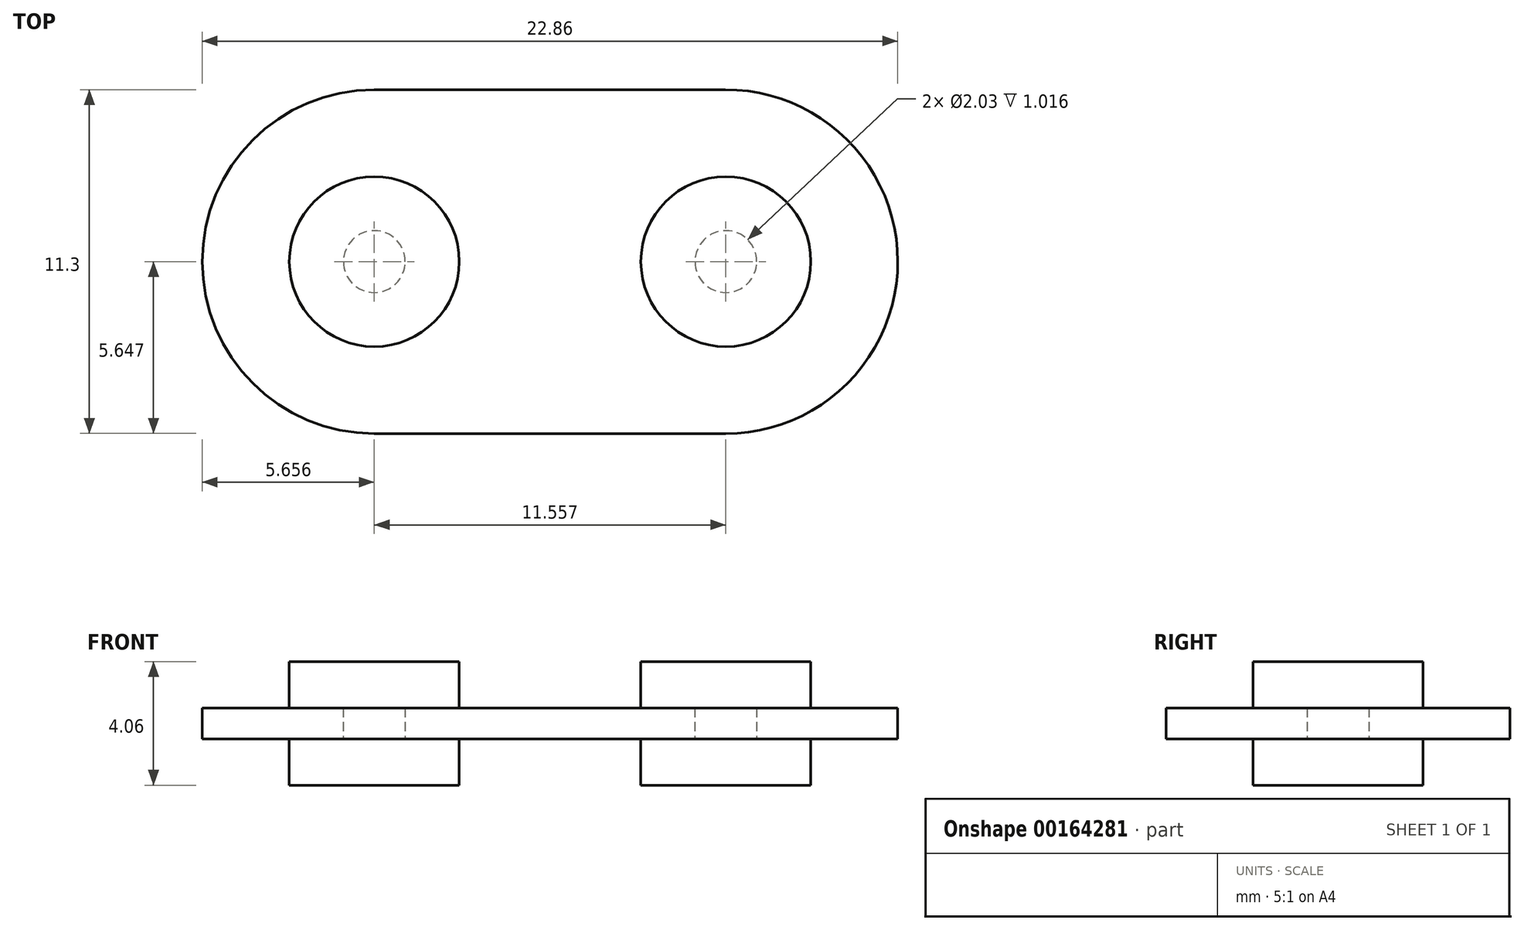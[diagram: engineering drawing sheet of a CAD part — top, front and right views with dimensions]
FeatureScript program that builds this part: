
annotation { "Feature Type Name" : "Feature", "Feature Type Description" : "" }
export const myFeature = defineFeature(function(context is Context, id is Id, definition is map)
    precondition{}
    {
        {
            var Q0;
            Q0=qCreatedBy(makeId("Top.planeOp"),FACE);
            var sketch = newSketch(context, id + "F0", { "sketchPlane" : qUnion([Q0])});
            skArc(sketch, "E0", {"start": v(4.5, -6.6) * mm, "mid": v(10.14, -0.93) * mm, "end": v(4.48, 4.7) * mm});
            skArc(sketch, "E1", {"start": v(-7.06, 4.7) * mm, "mid": v(-12.72, -0.94) * mm, "end": v(-7.06, -6.6) * mm});
            skLineSegment(sketch, "E2", {"start": v(-7.06, 4.7) * mm, "end": v(4.51, 4.7) * mm});
            skLineSegment(sketch, "E3", {"start": v(-7.06, -6.6) * mm, "end": v(4.5, -6.6) * mm});
            skCircle(sketch, "E4", {"center": v(-7.06, -0.94) * mm, "radius": 1.02 * mm});
            skCircle(sketch, "E5", {"center": v(4.5, -0.94) * mm, "radius": 1.02 * mm});
            skLineSegment(sketch, "E6", {"start": v(4.5, -0.94) * mm, "end": v(4.5, 4.7) * mm, "construction": true});
            skPoint(sketch, "E6.endSnap0", {"position": v(-1.28, 4.7) * mm});
            skLineSegment(sketch, "E7", {"start": v(4.5, 4.7) * mm, "end": v(4.5, -6.6) * mm, "construction": true});
            skSolve(sketch);
        }
        {
            var Q0;
            Q0 = qSketchRegion(id + "F0", true);
            extrude(context, id + "F1", {"entities" : qUnion([Q0]), "depth" : 1.02 * mm});
        }
        {
            var Q0;
            Q0=makeQuery(id+"F1.opExtrude","CAP_FACE",FACE,{"disambiguationData":[OSD([sQuery(id+"F0.wireOp",EDGE,"E0"),sQuery(id+"F0.wireOp",EDGE,"E1"),sQuery(id+"F0.wireOp",EDGE,"E2"),sQuery(id+"F0.wireOp",EDGE,"E3"),sQuery(id+"F0.wireOp",EDGE,"E4"),sQuery(id+"F0.wireOp",EDGE,"E5")])],"isStart":false});
            var sketch = newSketch(context, id + "F2", { "sketchPlane" : qUnion([Q0])});
            skCircle(sketch, "E8", {"center": v(4.5, -0.94) * mm, "radius": 2.8 * mm});
            skCircle(sketch, "E9", {"center": v(-7.06, -0.94) * mm, "radius": 2.8 * mm});
            skSolve(sketch);
        }
        {
            var Q0;
            Q0 = qSketchRegion(id + "F2", true);
            extrude(context, id + "F3", {"entities" : qUnion([Q0]), "operationType" : NewBodyOperationType.ADD, "depth" : 1.52 * mm});
        }
        {
            var Q0;
            Q0=makeQuery(id+"F1.opExtrude","CAP_FACE",FACE,{"disambiguationData":[OSD([sQuery(id+"F0.wireOp",EDGE,"E0"),sQuery(id+"F0.wireOp",EDGE,"E1"),sQuery(id+"F0.wireOp",EDGE,"E2"),sQuery(id+"F0.wireOp",EDGE,"E3"),sQuery(id+"F0.wireOp",EDGE,"E4"),sQuery(id+"F0.wireOp",EDGE,"E5")])],"isStart":true});
            var sketch = newSketch(context, id + "F4", { "sketchPlane" : qUnion([Q0])});
            skCircle(sketch, "E10", {"center": v(4.5, 0.94) * mm, "radius": 2.8 * mm});
            skCircle(sketch, "E11", {"center": v(-7.06, 0.94) * mm, "radius": 2.8 * mm});
            skSolve(sketch);
        }
        {
            var Q0;
            Q0 = qSketchRegion(id + "F4", true);
            extrude(context, id + "F5", {"entities" : qUnion([Q0]), "operationType" : NewBodyOperationType.ADD, "depth" : 1.52 * mm});
        }
    });
